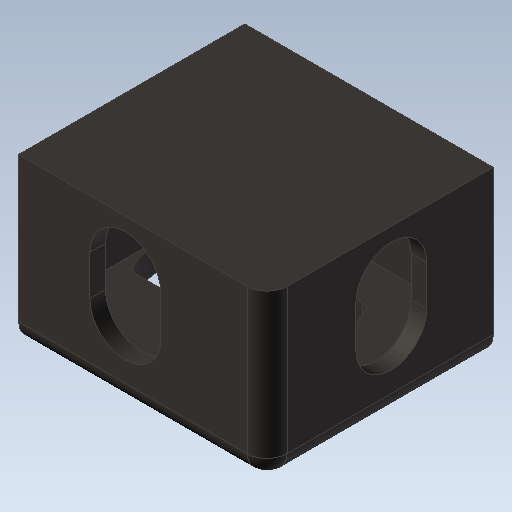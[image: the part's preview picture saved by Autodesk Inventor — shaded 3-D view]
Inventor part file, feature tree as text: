
AUTODESK INVENTOR PART (.ipt)
format: ipt  version: 2020 (Build 240168000, 168)  size: 163,328 bytes
history: mixed  units: mm
features: fillet x1, imported_body x1
ambient origin geometry x8: Origin, YZ Plane, XZ Plane, XY Plane, X Axis, Y Axis, Z Axis, Center Point
bodies: Solid1 (imported_parasolid)
feature tree (2):
  fillet  "Fillet1"  [1 undecoded]
  imported_body  NMx_Import_Brep_tag  [imported B-rep: ~42 faces, bbox_mm=[178.0, 118.0, 162.0]]
note: 1 required parameter value undecoded (feature->parameter linkage not recoverable at this tier; creation-order binding heuristic only, values carry confidence <= 0.55)
